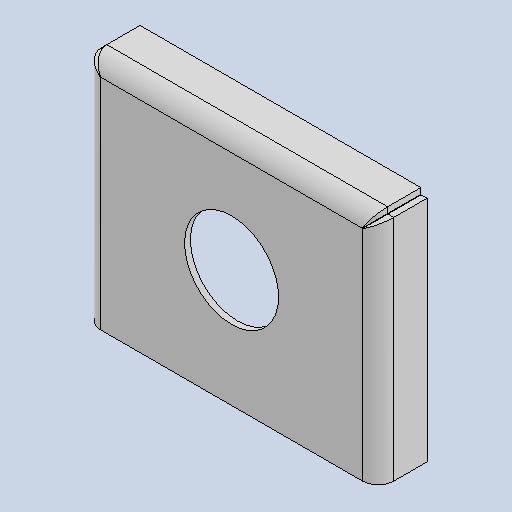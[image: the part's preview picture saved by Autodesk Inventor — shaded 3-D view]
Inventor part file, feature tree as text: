
AUTODESK INVENTOR PART (.ipt)
format: ipt  version: 2025 (Build 290162010, 162A)  size: 235,008 bytes
history: native  units: mm
features: sketch x4, extrude x3, other x3, sheet_metal_op x3
ambient origin geometry x8: Origin, YZ Plane, XZ Plane, XY Plane, X Axis, Y Axis, Z Axis, Center Point
bodies: Solid1 (feature_tree)
feature tree (13):
  extrude  "Extrusion1"  Depth=3.0mm TaperAngle=0.0deg
  other  "A-Side Definition"
  sheet_metal_op  "Flange1"
  extrude  "Extrusion2"  Depth=120.0mm
  extrude  "Extrusion3"  Depth=3.0mm
  sketch  "Sketch1"  dims[d4=150.0mm d5=3.0mm d6=0.0mm]
  sketch  "Sketch2"  dims[d13=48.1mm d14=120.0mm]
  other  "Plate1"
  sheet_metal_op  "Bend1"
  sheet_metal_op  "Corner1"
  sketch  "Sketch3"  dims[d15=60.0mm d16=3.0mm]
  sketch  "Sketch4"  dims[d17=3.0mm d18=1.5mm d19=6.0mm d20=5.0mm d21=25.0mm d22=90.0deg d23=5.0mm d24=12.0mm d25=0.2mm d26=5.0mm d27=6.0mm d28=60.0mm d29=0.0mm d30=0.0mm d31=6.0mm d32=60.0mm d34=0.0mm d35=0.0mm d33=0.5mm]
  other  "Definition1"
